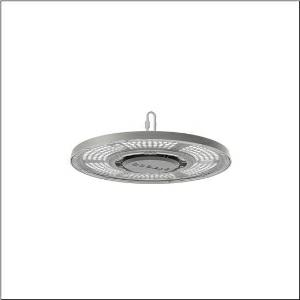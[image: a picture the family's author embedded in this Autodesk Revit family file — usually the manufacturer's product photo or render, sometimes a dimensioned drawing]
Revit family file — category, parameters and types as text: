
# Revit family: highbay_31-s_51hc417a4jmb
name_source: partatom
category: Lighting Fixtures
units: mm (PartAtom-declared; Revit-internal decimal feet)

## family parameters
Cut with Voids When Loaded = No
Host = Face
Light Source = No
Part Type = Normal
Room Calculation Point = No
Round Connector Dimension = Use Diameter
Shared = No

## types (1)
- Highbay 31-S (1 x LED, 20000 lm, 134 W, 4000K)
    Apparent Load = 134 VA
    CIE Flux Codes = 95 98 100 100 100
    Color Rendering = 80
    Color Temperature = 4000K
    Default Elevation = 1800 mm
    Description = Highbay 31-S, high bay luminaire, primary light control with lens, of PC, primary optical cover: cover panel, of PC, transparent, light emission: direct distribution, primary light characteristic: rotationally symmetric, installation type: suspended mounting, surface-mounted, LED, rated luminous flux: 20.000lm, luminous efficacy: 150lm/W, light colour: 840, colour temperature: 4000K, control gear: ON/OFF, with cable, 3x 1.0mm², free wire ends, mains connection: 220..240V, AC/DC, 0/50..60Hz, cable length: 1,5m, rated input power: 134W, housing, rotationally symmetric, of diecast aluminium, powder-coated, grey aluminium (RAL 9007), with hook on luminaire side, incl. screw, diameter: 339mm, protection rating (complete): IP65, insulation class (complete): insulation class I (protective earthing), certification: CE, ENEC, UKCA, protection symbol: D, impact resistance: IK08, permissible operating ambient temperature: -30..+45°C, standard: EN 60598-2-22, EN 60598, corresponds to IFS (International Featured Standards) requirements for safety and quality in the food industry, packaging unit: 1 piece
    Height = 141 mm
    Lamp = 1 x LED
    Lamp Light Flux = 20000 lm
    Lamp Power = 134 W
    Lamp count = 1
    Length = 339 mm
    Luminous efficacy = 149 lm/W
    Manufacturer = Siteco
    ModVariant = No
    Model = 51HC417A4JMB
    Mounting Place = Ceiling
    Mounting Type = Pendant
    Number of Poles = 1
    OnlyDefault = Yes
    Power Factor = 1
    Product Name = Highbay 31-S
    Product group = high bay luminaire
    ProductGroupID = 901
    Protection Class = Protection class I
    Protection Degree = IP 65
    RLX_Detail_Level = 1
    RLX_Emergency_Light_Flux = 0 lm
    RLX_Emergency_Type = 0
    RLX_Emergency_Type_DB = No
    RlxData = <blob elided: 106533 chars, md5=f2509cf8>
    Socket = socket
    Standby Power = 0 W
    System Light Flux = 20000 lm
    System Power = 134 W
    Type Comments = Product without accessories
    Type Image = l_1007237.jpg
    URL = http://relux.com
    VarID = ---
    Voltage = 0 V
    Weight = 0.00 kg
    Width = 0 mm  [stored 0 ft]

note: [stored X ft] marks values corroborated as IEEE doubles in the binary element streams (Revit-internal decimal feet)

## geometry (parser evidence)
native form markers: Blend x4, Sweep x9
no freeform markers — native parametric forms only
